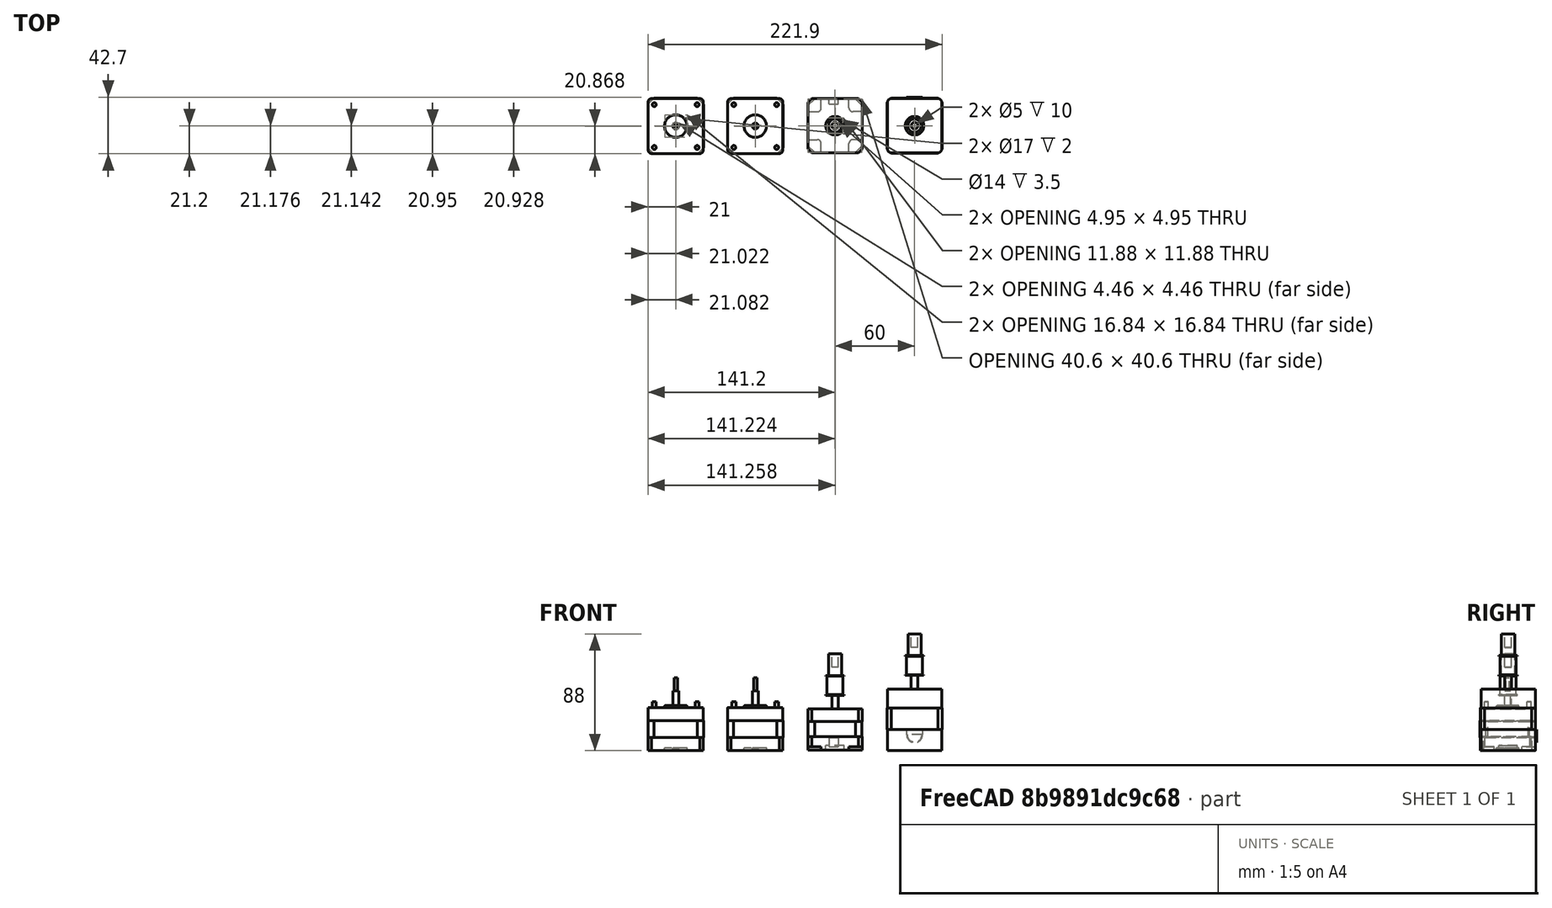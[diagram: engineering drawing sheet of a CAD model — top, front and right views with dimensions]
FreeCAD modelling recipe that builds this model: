
FCSTD DOCUMENT  (FreeCAD 0.15R4671 (Git))
Label: Motores Y_E_Z
License: All rights reserved
LicenseURL: http://en.wikipedia.org/wiki/All_rights_reserved
objects: Part::Cylinder×21, Part::Cut×15, Part::Box×14, Part::MultiFuse×12, Part::Fillet×8, Part::Chamfer×7, Part::Fuse×1
note: 78 computed .brp shape members not serialized (recipe doc carries the construction recipe); baked Part::Feature solids carry a one-line shape summary decoded from their .brp

FEATURE [Part::Box] Box  label="Cubo086"
  Height = 32.5
  Length = 41.5
  Placement = pos=(-55,-43,0) rot=(0,0,1;0rad)
  Width = 41.5
FEATURE [Part::Box] Box001  label="Cubo087"
  Height = 12.5
  Length = 44.5
  Placement = pos=(-56,-44,10) rot=(0,0,1;0rad)
  Width = 44.5
FEATURE [Part::Box] Box002  label="Cubo088"
  Height = 12.5
  Length = 41.9
  Placement = pos=(-55.2,-43.2,10) rot=(0,0,1;0rad)
  Width = 41.9
FEATURE [Part::Cut] Cut
  Base = -> Box
  Tool = -> Box001
FEATURE [Part::Fillet] Fillet
  Base = -> Cut
  Edges = 4 edges r=2.5: [Edge18,Edge19,Edge21,Edge23]
FEATURE [Part::Chamfer] Chamfer
  Base = -> Fillet
  Edges = 4 edges r=2.5: [Edge29,Edge30,Edge32,Edge34]
FEATURE [Part::Chamfer] Chamfer001
  Base = -> Box002
  Edges = 4 edges r=4.5: [Edge1,Edge3,Edge5,Edge7]
FEATURE [Part::Cylinder] Cylinder  label="Cilindro034"
  Angle = 360
  Height = 45
  Placement = pos=(-34.2,-22.25,0) rot=(0,0,1;0rad)
  Radius = 2.25
FEATURE [Part::Cylinder] Cylinder001  label="Cilindro035"
  Angle = 360
  Height = 32
  Placement = pos=(-34.2,-22.25,2) rot=(0,0,1;0rad)
  Radius = 8.5
FEATURE [Part::Cylinder] Cylinder002  label="Cilindro036"
  Angle = 360
  Height = 3
  Placement = pos=(-34.2,-22.25,-1) rot=(0,0,1;0rad)
  Radius = 8.5
FEATURE [Part::MultiFuse] Fusion
  Shapes = -> [Chamfer001,Chamfer]
FEATURE [Part::Fillet] Fillet001
  Base = -> Cylinder001
  Edges = 1 edges r=0.6: [Edge1]
FEATURE [Part::Cut] Cut001
  Base = -> Fusion
  Tool = -> Cylinder002
FEATURE [Part::Cylinder] Cylinder003  label="Cilindro037"
  Angle = 360
  Height = 10
  Placement = pos=(-34.2,-22.25,45) rot=(0,0,1;0rad)
  Radius = 1.25
FEATURE [Part::Cylinder] Cylinder004  label="tornillo017"
  Angle = 360
  Height = 10
  Placement = pos=(-18.1,-38.4,27) rot=(0,0,1;0rad)
  Radius = 1.5
FEATURE [Part::Cylinder] Cylinder005  label="tornillo018"
  Angle = 360
  Height = 10
  Placement = pos=(-50.4,-38.4,27) rot=(0,0,1;0rad)
  Radius = 1.5
FEATURE [Part::Cylinder] Cylinder006  label="tornillo019"
  Angle = 360
  Height = 10
  Placement = pos=(-18.1,-6.1,27) rot=(0,0,1;0rad)
  Radius = 1.5
FEATURE [Part::Cylinder] Cylinder007  label="tornillo020"
  Angle = 360
  Height = 10
  Placement = pos=(-50.4,-6.1,27) rot=(0,0,1;0rad)
  Radius = 1.5
FEATURE [Part::MultiFuse] Fusion002  label="motor extrusor003"
  Shapes = -> [Cylinder,Fillet001,Cut001,Cylinder003]
FEATURE [Part::MultiFuse] Fusion001  label="EjeY_motor"
  Shapes = -> [Fusion002,Cylinder007,Cylinder006,Cylinder005,Cylinder004]
FEATURE [Part::Fuse] Fusion003  label="motor eje Z grande"
  Placement = pos=(-20.5,-20.5,0) rot=(0,0,1;0rad)
FEATURE [Part::Cylinder] Cylinder008  label="fuera"
  Angle = 360
  Height = 14.9
  Placement = pos=(0,0,56.8) rot=(0,0,1;0rad)
  Radius = 7
FEATURE [Part::Cylinder] Cylinder009  label="interior resta"
  Angle = 360
  Height = 14
  Placement = pos=(0,0,57.3) rot=(0,0,1;0rad)
  Radius = 10.3
FEATURE [Part::Cut] Cut002
  Base = -> Cylinder008
  Tool = -> Cylinder009
FEATURE [Part::Cut] Cut003  label="CABLES MOTOR Z 2"
  Placement = pos=(0,-0.5,0) rot=(0,0,1;0rad)
FEATURE [Part::MultiFuse] Fusion004  label="eje completo Motor Z2"
FEATURE [Part::MultiFuse] Fusion005  label="EjeZ_Motor_Derecha"
  Placement = pos=(146,-22,0) rot=(0,0,1;0rad)
  Shapes = -> [Fusion003,Fusion004,Cut003]
FEATURE [Part::Box] Box003  label="Cubo063"
  Height = 31
  Length = 41
  Placement = pos=(1,0,-137.5) rot=(0,0,1;0rad)
  Width = 41
FEATURE [Part::Box] Box004  label="resta001"
  Height = 11.5
  Length = 51
  Placement = pos=(-5,-5,-127.5) rot=(0,0,1;0rad)
  Width = 50
FEATURE [Part::Chamfer] Chamfer002  label="parte gris001"
  Base = -> Box003
  Edges = 4 edges r=3: [Edge1,Edge3,Edge5,Edge7]
FEATURE [Part::Chamfer] Chamfer003  label="resta002"
  Base = -> Box004
  Edges = 4 edges r=5: [Edge1,Edge3,Edge5,Edge7]
FEATURE [Part::Box] Box005  label="resta004"
  Height = 11.5
  Length = 40.6
  Placement = pos=(1,0,-127.5) rot=(0,0,1;0rad)
  Width = 40.6
FEATURE [Part::Chamfer] Chamfer004  label="verde"
  Base = -> Box005
  Edges = 4 edges r=5: [Edge1,Edge3,Edge5,Edge7]
  Placement = pos=(0.2,0.2,0) rot=(0,0,1;0rad)
FEATURE [Part::Cut] Cut004
  Base = -> Chamfer002
  Tool = -> Chamfer003
FEATURE [Part::Box] Box006  label="cables"
  Height = 7
  Length = 7
  Placement = pos=(17,37,-135) rot=(0,0,1;0rad)
  Width = 7
FEATURE [Part::Cut] Cut005
  Base = -> Cut004
  Tool = -> Box006
FEATURE [Part::Cut] Cut006  label="agarrra varilla eje Z 003"
  Placement = pos=(0,0,-1) rot=(0,0,1;0rad)
FEATURE [Part::MultiFuse] Fusion006  label="polea abajo motor Z 003"
  Shapes = -> [Cut002]
FEATURE [Part::Cylinder] Cylinder010  label="Cilindro019"
  Angle = 360
  Height = 73
  Radius = 2.5
FEATURE [Part::MultiFuse] Fusion007  label="eje completo Motor Z004"
  Placement = pos=(21,21,-153) rot=(0,0,1;0rad)
  Shapes = -> [Cylinder010,Fusion006,Cut006]
FEATURE [Part::MultiFuse] Fusion008  label="Motor Z1"
  Placement = pos=(-0.5,0.5,0) rot=(0,0,1;0rad)
  Shapes = -> [Chamfer004,Cut005]
FEATURE [Part::Cylinder] Cylinder011  label="BORRA "
  Angle = 360
  Height = 22
  Placement = pos=(21,21,-155) rot=(0,0,1;0rad)
  Radius = 5
FEATURE [Part::Cut] Cut007  label="EJE MOTOR Z1"
  Base = -> Fusion007
  Tool = -> Cylinder011
FEATURE [Part::MultiFuse] Fusion009  label="Motor Z 1"
  Placement = pos=(-47,11,0) rot=(0,0,1;0rad)
  Shapes = -> [Cut007,Fusion008]
FEATURE [Part::Box] Box007  label="extremos abajo"
  Height = 3
  Length = 11
  Placement = pos=(-47.5,10.5,-138) rot=(0,0,1;0rad)
  Width = 11
FEATURE [Part::Box] Box008  label="extremos abajo001"
  Height = 3
  Length = 11
  Placement = pos=(-47.5,42.5,-138) rot=(0,0,1;0rad)
  Width = 11
FEATURE [Part::Box] Box009  label="extremos abajo002"
  Height = 3
  Length = 11
  Placement = pos=(-15.5,10.5,-138) rot=(0,0,1;0rad)
  Width = 11
FEATURE [Part::Box] Box010  label="extremos abajo003"
  Height = 3
  Length = 11
  Placement = pos=(-15.5,42.5,-138) rot=(0,0,1;0rad)
  Width = 11
FEATURE [Part::Fillet] Fillet002
  Base = -> Box008
  Edges = 1 edges r=3: [Edge5]
FEATURE [Part::Fillet] Fillet003
  Base = -> Box009
  Edges = 1 edges r=3: [Edge3]
FEATURE [Part::Fillet] Fillet004
  Base = -> Box010
  Edges = 1 edges r=3: [Edge1]
FEATURE [Part::Fillet] Fillet005
  Base = -> Box007
  Edges = 1 edges r=3: [Edge7]
FEATURE [Part::Cylinder] Cylinder012  label="agujero abajo motor z1"
  Angle = 360
  Height = 10
  Placement = pos=(-26,32,-144) rot=(0,0,1;0rad)
  Radius = 7
FEATURE [Part::Cut] Cut008
  Base = -> Fusion009
  Tool = -> Fillet002
FEATURE [Part::Cut] Cut009
  Base = -> Cut008
  Tool = -> Fillet003
FEATURE [Part::Cut] Cut010
  Base = -> Cut009
  Tool = -> Fillet004
FEATURE [Part::Cut] Cut011
  Base = -> Cut010
  Tool = -> Fillet005
FEATURE [Part::Cut] Cut012  label="EjeZ_Motor_Izquierda"
  Base = -> Cut011
  Placement = pos=(112,-54,138) rot=(0,0,1;0rad)
  Tool = -> Cylinder012
FEATURE [Part::Box] Box011  label="Cubo089"
  Height = 32.5
  Length = 41.5
  Placement = pos=(-55,-43,0) rot=(0,0,1;0rad)
  Width = 41.5
FEATURE [Part::Box] Box012  label="Cubo090"
  Height = 12.5
  Length = 44.5
  Placement = pos=(-56,-44,10) rot=(0,0,1;0rad)
  Width = 44.5
FEATURE [Part::Box] Box013  label="Cubo091"
  Height = 12.5
  Length = 41.9
  Placement = pos=(-55.2,-43.2,10) rot=(0,0,1;0rad)
  Width = 41.9
FEATURE [Part::Cut] Cut013
  Base = -> Box011
  Tool = -> Box012
FEATURE [Part::Fillet] Fillet006
  Base = -> Cut013
  Edges = 4 edges r=2.5: [Edge18,Edge19,Edge21,Edge23]
FEATURE [Part::Chamfer] Chamfer005
  Base = -> Fillet006
  Edges = 4 edges r=2.5: [Edge29,Edge30,Edge32,Edge34]
FEATURE [Part::Chamfer] Chamfer006
  Base = -> Box013
  Edges = 4 edges r=4.5: [Edge1,Edge3,Edge5,Edge7]
FEATURE [Part::Cylinder] Cylinder013  label="Cilindro038"
  Angle = 360
  Height = 45
  Placement = pos=(-34.2,-22.25,0) rot=(0,0,1;0rad)
  Radius = 2.25
FEATURE [Part::Cylinder] Cylinder014  label="Cilindro039"
  Angle = 360
  Height = 32
  Placement = pos=(-34.2,-22.25,2) rot=(0,0,1;0rad)
  Radius = 8.5
FEATURE [Part::Cylinder] Cylinder015  label="Cilindro040"
  Angle = 360
  Height = 3
  Placement = pos=(-34.2,-22.25,-1) rot=(0,0,1;0rad)
  Radius = 8.5
FEATURE [Part::MultiFuse] Fusion010
  Shapes = -> [Chamfer006,Chamfer005]
FEATURE [Part::Fillet] Fillet007
  Base = -> Cylinder014
  Edges = 1 edges r=0.6: [Edge1]
FEATURE [Part::Cut] Cut014
  Base = -> Fusion010
  Tool = -> Cylinder015
FEATURE [Part::Cylinder] Cylinder016  label="Cilindro041"
  Angle = 360
  Height = 10
  Placement = pos=(-34.2,-22.25,45) rot=(0,0,1;0rad)
  Radius = 1.25
FEATURE [Part::MultiFuse] Fusion011  label="motor extrusor"
  Shapes = -> [Cylinder013,Fillet007,Cut014,Cylinder016]
FEATURE [Part::Cylinder] Cylinder017  label="tornillo011"
  Angle = 360
  Height = 10
  Placement = pos=(-18.1,-6.1,27) rot=(0,0,1;0rad)
  Radius = 1.5
FEATURE [Part::Cylinder] Cylinder018  label="tornillo013"
  Angle = 360
  Height = 10
  Placement = pos=(-50.4,-6.1,27) rot=(0,0,1;0rad)
  Radius = 1.5
FEATURE [Part::Cylinder] Cylinder019  label="tornillo014"
  Angle = 360
  Height = 10
  Placement = pos=(-50.4,-38.4,27) rot=(0,0,1;0rad)
  Radius = 1.5
FEATURE [Part::Cylinder] Cylinder020  label="tornillo016"
  Angle = 360
  Height = 10
  Placement = pos=(-18.1,-38.4,27) rot=(0,0,1;0rad)
  Radius = 1.5
FEATURE [Part::MultiFuse] Fusion012  label="motor repuesto"
  Placement = pos=(60,0,0) rot=(0,0,1;0rad)
  Shapes = -> [Fusion011,Cylinder018,Cylinder017,Cylinder019,Cylinder020]
